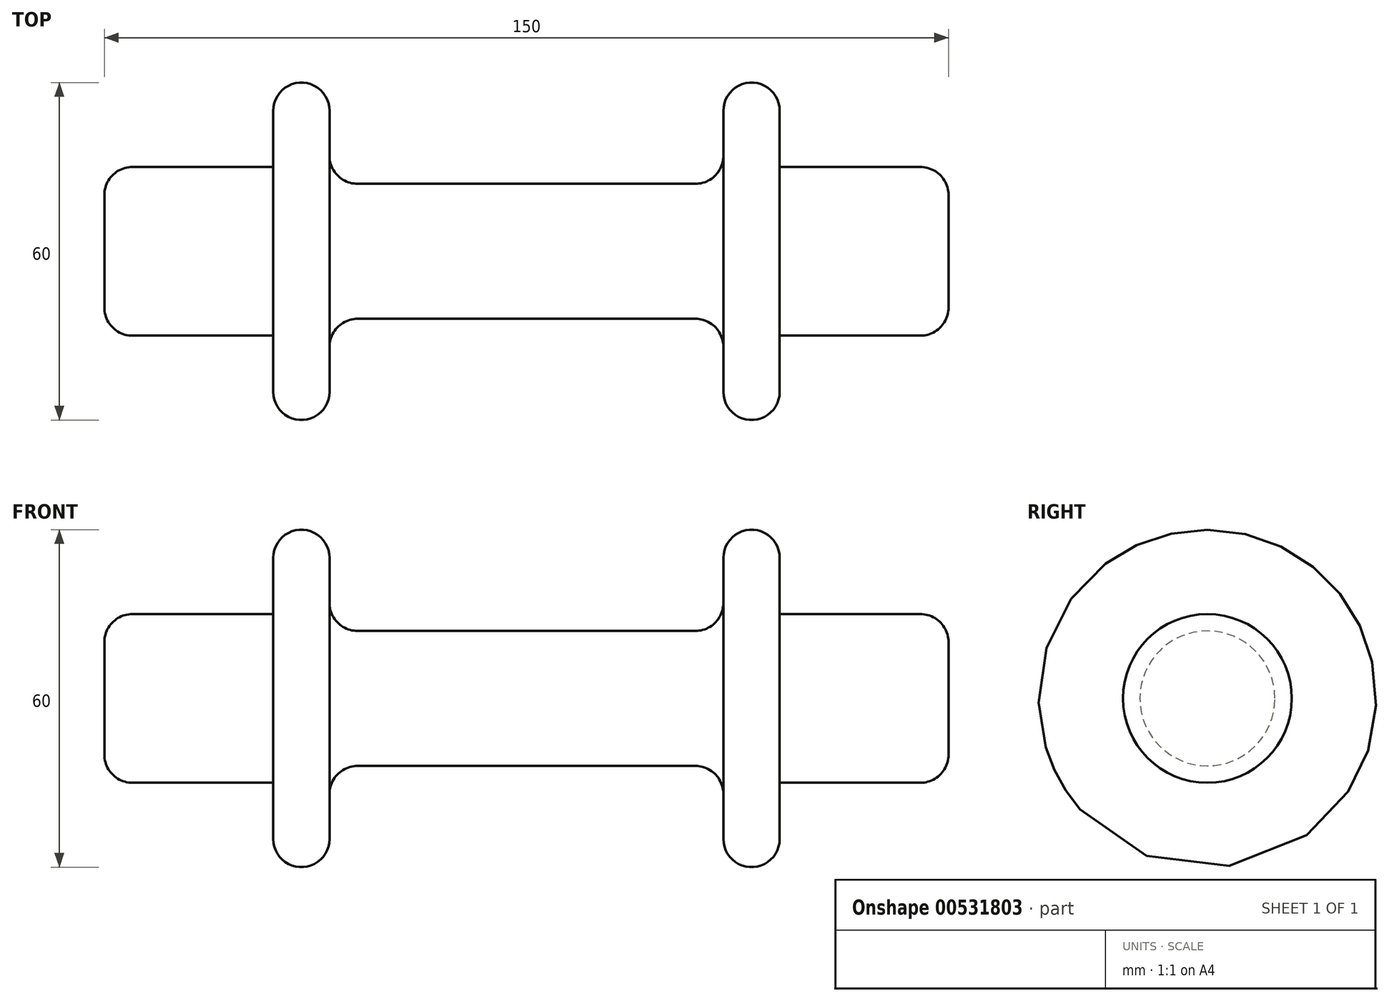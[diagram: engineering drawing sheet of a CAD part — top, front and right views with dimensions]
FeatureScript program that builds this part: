
annotation { "Feature Type Name" : "Feature", "Feature Type Description" : "" }
export const myFeature = defineFeature(function(context is Context, id is Id, definition is map)
    precondition{}
    {
        {
            var Q0;
            Q0=qCreatedBy(makeId("Front.planeOp"),FACE);
            var sketch = newSketch(context, id + "F0", { "sketchPlane" : qUnion([Q0])});
            skLineSegment(sketch, "E0", {"start": v(0, 12) * mm, "end": v(30, 12) * mm});
            skLineSegment(sketch, "E1", {"start": v(35, 17) * mm, "end": v(35, 30) * mm});
            skLineSegment(sketch, "E2", {"start": v(35, 30) * mm, "end": v(45, 30) * mm});
            skLineSegment(sketch, "E3", {"start": v(45, 30) * mm, "end": v(45, 15) * mm});
            skLineSegment(sketch, "E4", {"start": v(45, 15) * mm, "end": v(75, 15) * mm});
            skLineSegment(sketch, "E5", {"start": v(75, 15) * mm, "end": v(75, 0) * mm});
            skLineSegment(sketch, "E6", {"start": v(75, 0) * mm, "end": v(0, 0) * mm});
            skLineSegment(sketch, "E7", {"start": v(0, 0) * mm, "end": v(0, 12) * mm});
            skPoint(sketch, "E8.visualSharp", {"position": v(35, 12) * mm});
            skArc(sketch, "E8.filletArc", {"start": v(30, 12) * mm, "mid": v(33.54, 13.46) * mm, "end": v(35, 17) * mm});
            skSolve(sketch);
        }
        {
            var Q0;
            Q0=makeQuery(id+"F0.imprint","IMPRINT",FACE,{"disambiguationData":[TD([[makeQuery(id+"F0.imprint","IMPRINT",EDGE,{"derivedFrom":sQuery(id+"F0.wireOp",EDGE,"E0")}),-1.0]])]});
            var Q1;
            Q1=sQuery(id+"F0.wireOp",EDGE,"E6");
            revolve(context, id + "F1", {"entities" : qUnion([Q0]), "axis" : qUnion([Q1]), "revolveType" : RevolveType.FULL});
        }
        {
            var Q0;
            Q0=makeQuery(id+"F1.opRevolve","SWEPT_BODY",BODY,{"disambiguationData":[OSD([sQuery(id+"F0.wireOp",EDGE,"E0"),sQuery(id+"F0.wireOp",EDGE,"E1"),sQuery(id+"F0.wireOp",EDGE,"E2"),sQuery(id+"F0.wireOp",EDGE,"E3"),sQuery(id+"F0.wireOp",EDGE,"E4"),sQuery(id+"F0.wireOp",EDGE,"E5"),sQuery(id+"F0.wireOp",EDGE,"E6"),sQuery(id+"F0.wireOp",EDGE,"E7"),sQuery(id+"F0.wireOp",EDGE,"E8.filletArc")])]});
            var Q1;
            Q1=makeQuery(id+"F1.opRevolve","SWEPT_FACE",FACE,{"disambiguationData":[OSD([sQuery(id+"F0.wireOp",EDGE,"E7")])]});
            mirror(context, id + "F2", {"operationType" : NewBodyOperationType.ADD, "entities" : qUnion([Q0]), "mirrorPlane" : qUnion([Q1])});
        }
        {
            var Q0;
            Q0=makeQuery(id+"F1.opRevolve","SWEPT_EDGE",EDGE,{"disambiguationData":[OSD([sQuery(id+"F0.wireOp",EDGE,"E4"),sQuery(id+"F0.wireOp",EDGE,"E5")])]});
            var Q1;
            Q1=makeQuery(id+"F2.opPattern","COPY",EDGE,{"derivedFrom":makeQuery(id+"F1.opRevolve","SWEPT_EDGE",EDGE,{"disambiguationData":[OSD([sQuery(id+"F0.wireOp",EDGE,"E4"),sQuery(id+"F0.wireOp",EDGE,"E5")])]}),"instanceName":"1"});
            var Q2;
            Q2=makeQuery(id+"F2.opPattern","COPY",EDGE,{"derivedFrom":makeQuery(id+"F1.opRevolve","SWEPT_EDGE",EDGE,{"disambiguationData":[OSD([sQuery(id+"F0.wireOp",EDGE,"E1"),sQuery(id+"F0.wireOp",EDGE,"E2")])]}),"instanceName":"1"});
            var Q3;
            Q3=makeQuery(id+"F2.opPattern","COPY",EDGE,{"derivedFrom":makeQuery(id+"F1.opRevolve","SWEPT_EDGE",EDGE,{"disambiguationData":[OSD([sQuery(id+"F0.wireOp",EDGE,"E2"),sQuery(id+"F0.wireOp",EDGE,"E3")])]}),"instanceName":"1"});
            var Q4;
            Q4=makeQuery(id+"F1.opRevolve","SWEPT_EDGE",EDGE,{"disambiguationData":[OSD([sQuery(id+"F0.wireOp",EDGE,"E2"),sQuery(id+"F0.wireOp",EDGE,"E3")])]});
            var Q5;
            Q5=makeQuery(id+"F1.opRevolve","SWEPT_EDGE",EDGE,{"disambiguationData":[OSD([sQuery(id+"F0.wireOp",EDGE,"E1"),sQuery(id+"F0.wireOp",EDGE,"E2")])]});
            var Q6;
            {var subQ0=makeQuery(id+"F1.opRevolve","SWEPT_FACE",FACE,{"disambiguationData":[OSD([sQuery(id+"F0.wireOp",EDGE,"E0")])]});Q6=makeQuery(id+"F2.boolean.opBoolean","MERGE",FACE,{"derivedFrom":[subQ0,makeQuery(id+"F2.opPattern","COPY",FACE,{"derivedFrom":subQ0,"instanceName":"1"})]});}
            fillet(context, id + "F3", {"entities" : qUnion([Q0, Q1, Q2, Q3, Q4, Q5, Q6]), "radius" : 5 * mm, "tangentPropagation" : true, "allowEdgeOverflow" : false});
        }
    });
